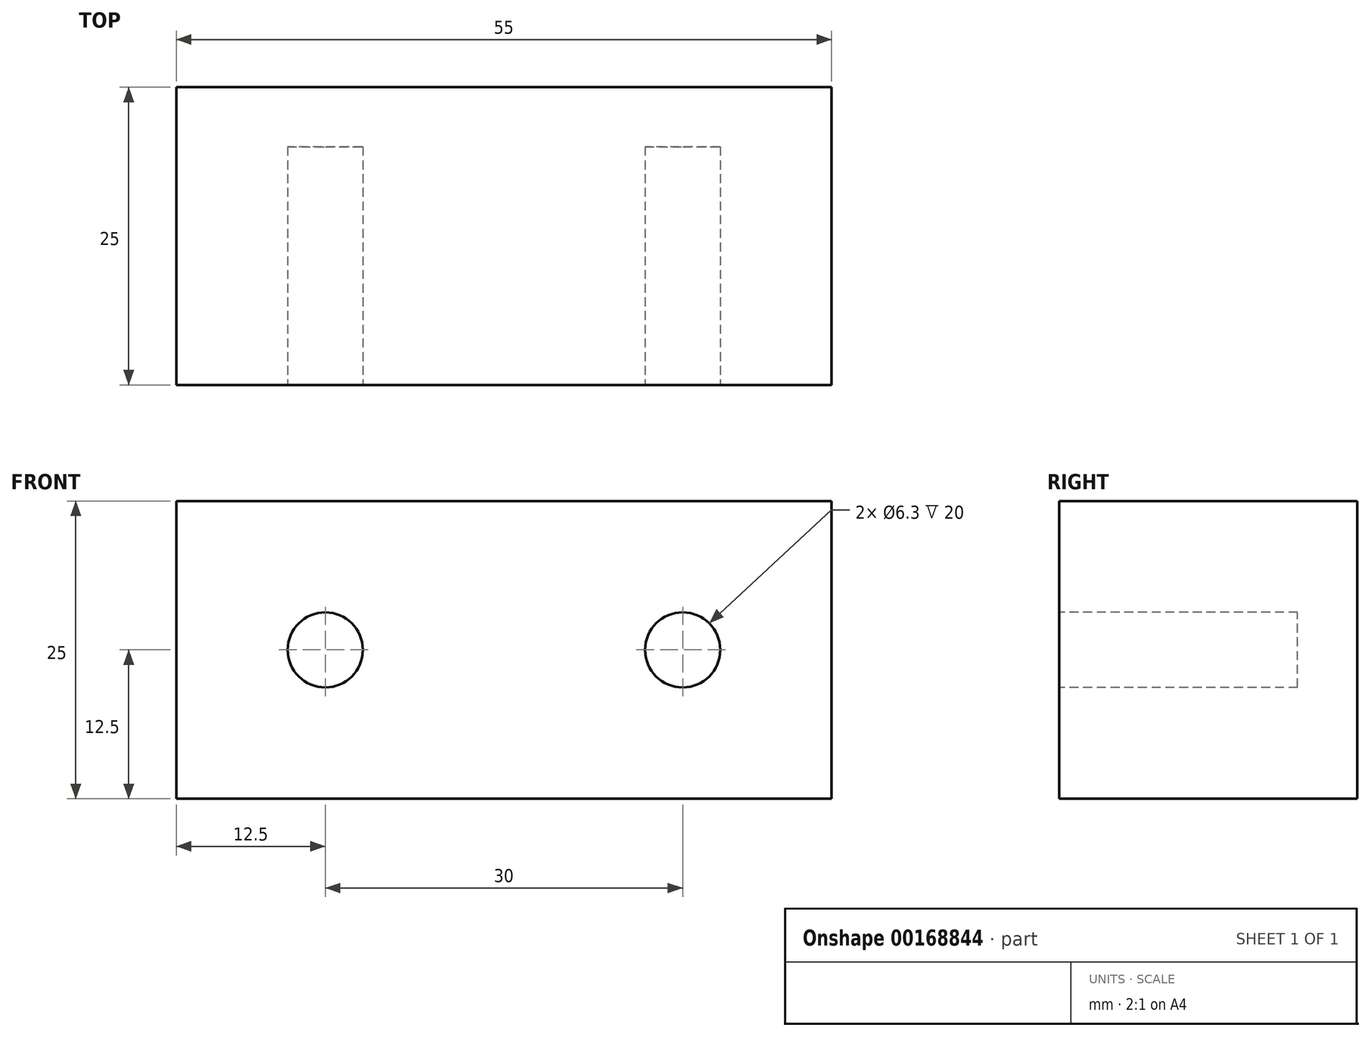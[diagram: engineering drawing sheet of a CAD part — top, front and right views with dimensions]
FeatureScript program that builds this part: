
annotation { "Feature Type Name" : "Feature", "Feature Type Description" : "" }
export const myFeature = defineFeature(function(context is Context, id is Id, definition is map)
    precondition{}
    {
        {
            var Q0;
            Q0=qCreatedBy(makeId("Front.planeOp"),FACE);
            var sketch = newSketch(context, id + "F0", { "sketchPlane" : qUnion([Q0])});
            skLineSegment(sketch, "E0.bottom", {"start": v(-27.5, -12.5) * mm, "end": v(27.5, -12.5) * mm});
            skLineSegment(sketch, "E0.top", {"start": v(-27.5, 12.5) * mm, "end": v(27.5, 12.5) * mm});
            skLineSegment(sketch, "E0.left", {"start": v(-27.5, -12.5) * mm, "end": v(-27.5, 12.5) * mm});
            skLineSegment(sketch, "E0.right", {"start": v(27.5, -12.5) * mm, "end": v(27.5, 12.5) * mm});
            skPoint(sketch, "E0.middle", {"position": v(0, 0) * mm});
            skSolve(sketch);
        }
        {
            var Q0;
            Q0=makeQuery(id+"F0.imprint","IMPRINT",FACE,{"disambiguationData":[TD([[makeQuery(id+"F0.imprint","IMPRINT",EDGE,{"derivedFrom":sQuery(id+"F0.wireOp",EDGE,"E0.bottom")}),1.0]])]});
            extrude(context, id + "F1", {"entities" : qUnion([Q0]), "depth" : 25 * mm});
        }
        {
            var Q0;
            Q0=makeQuery(id+"F1.opExtrude","CAP_FACE",FACE,{"disambiguationData":[OSD([sQuery(id+"F0.wireOp",EDGE,"E0.bottom"),sQuery(id+"F0.wireOp",EDGE,"E0.top"),sQuery(id+"F0.wireOp",EDGE,"E0.left"),sQuery(id+"F0.wireOp",EDGE,"E0.right")])],"isStart":false});
            var sketch = newSketch(context, id + "F2", { "sketchPlane" : qUnion([Q0])});
            skCircle(sketch, "E1", {"center": v(-15, 0) * mm, "radius": 3.15 * mm});
            skCircle(sketch, "E2", {"center": v(15, 0) * mm, "radius": 3.15 * mm});
            skSolve(sketch);
        }
        {
            var Q0;
            Q0=makeQuery(id+"F2.imprint","IMPRINT",FACE,{"disambiguationData":[TD([[makeQuery(id+"F2.imprint","IMPRINT",EDGE,{"derivedFrom":sQuery(id+"F2.wireOp",EDGE,"E1")}),1.0]])]});
            var Q1;
            Q1=makeQuery(id+"F2.imprint","IMPRINT",FACE,{"disambiguationData":[TD([[makeQuery(id+"F2.imprint","IMPRINT",EDGE,{"derivedFrom":sQuery(id+"F2.wireOp",EDGE,"E2")}),1.0]])]});
            extrude(context, id + "F3", {"entities" : qUnion([Q0, Q1]), "operationType" : NewBodyOperationType.REMOVE, "oppositeDirection" : true, "depth" : 20 * mm});
        }
    });
